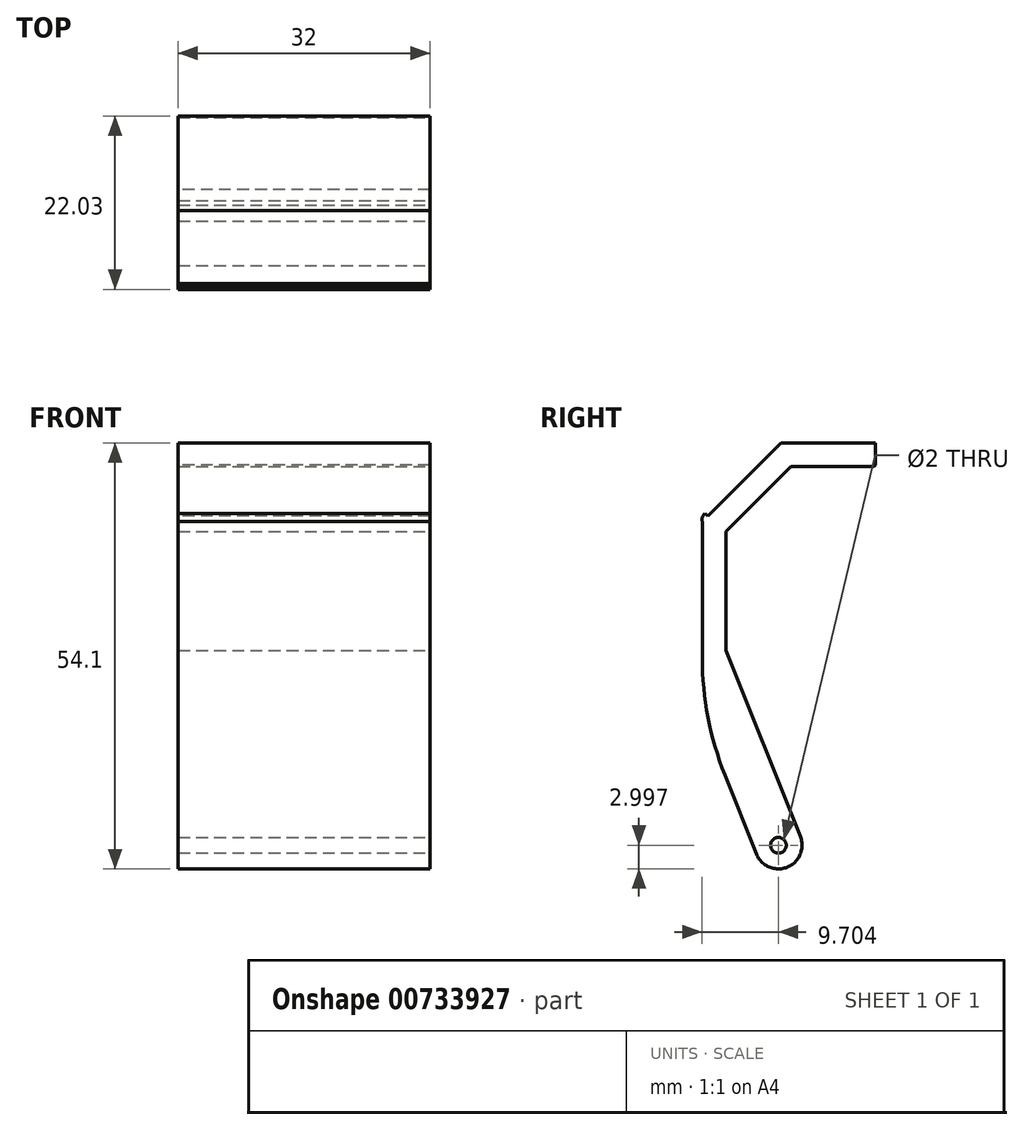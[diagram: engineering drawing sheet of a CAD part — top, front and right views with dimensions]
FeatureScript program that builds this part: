
annotation { "Feature Type Name" : "Feature", "Feature Type Description" : "" }
export const myFeature = defineFeature(function(context is Context, id is Id, definition is map)
    precondition{}
    {
        {
            var Q0;
            Q0=qCreatedBy(makeId("Right.planeOp"),FACE);
            var sketch = newSketch(context, id + "F0", { "sketchPlane" : qUnion([Q0])});
            skLineSegment(sketch, "E0.bottom", {"start": v(43.74, 41.65) * mm, "end": v(40.74, 41.65) * mm});
            skLineSegment(sketch, "E0.top", {"start": v(43.74, 21.65) * mm, "end": v(40.74, 21.65) * mm});
            skLineSegment(sketch, "E0.left", {"start": v(43.74, 41.65) * mm, "end": v(43.74, 21.65) * mm});
            skLineSegment(sketch, "E0.right", {"start": v(40.74, 41.65) * mm, "end": v(40.74, 21.65) * mm});
            skSolve(sketch);
        }
        {
            var Q0;
            Q0=makeQuery(id+"F0.imprint","IMPRINT",FACE,{"disambiguationData":[TD([[makeQuery(id+"F0.imprint","IMPRINT",EDGE,{"derivedFrom":sQuery(id+"F0.wireOp",EDGE,"E0.bottom")}),1.0]])]});
            extrude(context, id + "F1", {"entities" : qUnion([Q0]), "depth" : 10 * mm, "offsetDistance" : 25 * mm});
        }
        {
            var Q0;
            Q0=makeQuery(id+"F1.opExtrude","CAP_FACE",FACE,{"disambiguationData":[OSD([sQuery(id+"F0.wireOp",EDGE,"E0.bottom"),sQuery(id+"F0.wireOp",EDGE,"E0.top"),sQuery(id+"F0.wireOp",EDGE,"E0.left"),sQuery(id+"F0.wireOp",EDGE,"E0.right")])],"isStart":true});
            var sketch = newSketch(context, id + "F2", { "sketchPlane" : qUnion([Q0])});
            skLineSegment(sketch, "E1.bottom", {"start": v(-43.74, 41.65) * mm, "end": v(-18.74, 41.65) * mm});
            skLineSegment(sketch, "E1.top", {"start": v(-43.74, -18.35) * mm, "end": v(-18.74, -18.35) * mm});
            skLineSegment(sketch, "E1.left", {"start": v(-43.74, 41.65) * mm, "end": v(-43.74, -18.35) * mm});
            skLineSegment(sketch, "E1.right", {"start": v(-18.74, 41.65) * mm, "end": v(-18.74, -18.35) * mm});
            skLineSegment(sketch, "E2", {"start": v(-28.74, -18.35) * mm, "end": v(-18.74, 6.65) * mm});
            skLineSegment(sketch, "E3", {"start": v(-28.74, 41.65) * mm, "end": v(-18.74, 31.65) * mm});
            skSolve(sketch);
        }
        {
            var Q0;
            {var subQ4=makeQuery(id+"F1.opExtrude","CAP_EDGE",EDGE,{"disambiguationData":[OSD([sQuery(id+"F0.wireOp",EDGE,"E0.top")])],"isStart":true});Q0=makeQuery(id+"F2.imprint","IMPRINT",FACE,{"disambiguationData":[TD([[makeQuery(id+"F2.imprint","IMPRINT",EDGE,{"derivedFrom":subQ4}),1.0]])]});}
            var Q1;
            {var subQ3=sQuery(id+"F2.wireOp",EDGE,"E2");Q1=makeQuery(id+"F2.imprint","IMPRINT",FACE,{"disambiguationData":[TD([[makeQuery(id+"F2.imprint","IMPRINT",EDGE,{"derivedFrom":subQ3}),1.0]])]});}
            extrude(context, id + "F3", {"entities" : qUnion([Q0, Q1]), "operationType" : NewBodyOperationType.ADD, "depth" : 3 * mm, "offsetDistance" : 25 * mm});
        }
        {
            var Q0;
            Q0=makeQuery(id+"F1.opExtrude","CAP_FACE",FACE,{"disambiguationData":[OSD([sQuery(id+"F0.wireOp",EDGE,"E0.bottom"),sQuery(id+"F0.wireOp",EDGE,"E0.top"),sQuery(id+"F0.wireOp",EDGE,"E0.left"),sQuery(id+"F0.wireOp",EDGE,"E0.right")])],"isStart":false});
            extrude(context, id + "F4", {"entities" : qUnion([Q0]), "operationType" : NewBodyOperationType.REMOVE, "oppositeDirection" : true, "depth" : 10 * mm, "offsetDistance" : 25 * mm});
        }
        {
            var Q0;
            Q0=makeQuery(id+"F4.boolean.opBoolean","MERGE",FACE,{"derivedFrom":[makeQuery(id+"F3.opExtrude","CAP_FACE",FACE,{"disambiguationData":[OSD([sQuery(id+"F2.wireOp",EDGE,"E1.bottom"),sQuery(id+"F2.wireOp",EDGE,"E1.top"),sQuery(id+"F2.wireOp",EDGE,"E1.left"),sQuery(id+"F2.wireOp",EDGE,"E1.right"),sQuery(id+"F2.wireOp",EDGE,"E2"),sQuery(id+"F2.wireOp",EDGE,"E3")])],"isStart":true}),makeQuery(id+"F4.opExtrude","CAP_FACE",FACE,{"disambiguationData":[OSD([sQuery(id+"F0.wireOp",EDGE,"E0.bottom"),sQuery(id+"F0.wireOp",EDGE,"E0.top"),sQuery(id+"F0.wireOp",EDGE,"E0.left"),sQuery(id+"F0.wireOp",EDGE,"E0.right")])],"isStart":false})]});
            var sketch = newSketch(context, id + "F5", { "sketchPlane" : qUnion([Q0])});
            skLineSegment(sketch, "E4", {"start": v(26.74, -13.35) * mm, "end": v(43.74, -13.35) * mm});
            skLineSegment(sketch, "E5.bottom", {"start": v(43.74, 41.65) * mm, "end": v(40.74, 41.65) * mm});
            skLineSegment(sketch, "E5.top", {"start": v(43.74, 21.65) * mm, "end": v(40.74, 21.65) * mm});
            skLineSegment(sketch, "E5.left", {"start": v(43.74, 41.65) * mm, "end": v(43.74, 21.65) * mm});
            skLineSegment(sketch, "E5.right", {"start": v(40.74, 41.65) * mm, "end": v(40.74, 21.65) * mm});
            skLineSegment(sketch, "E6", {"start": v(25.74, 38.65) * mm, "end": v(40.74, 38.65) * mm});
            skLineSegment(sketch, "E7", {"start": v(21.74, 34.65) * mm, "end": v(21.74, -0.85) * mm});
            skLineSegment(sketch, "E8", {"start": v(28.74, 41.65) * mm, "end": v(18.74, 31.65) * mm});
            skLineSegment(sketch, "E9", {"start": v(28.74, 41.65) * mm, "end": v(34.27, 36.12) * mm});
            skLineSegment(sketch, "E10", {"start": v(18.74, 31.65) * mm, "end": v(24.45, 25.94) * mm});
            skLineSegment(sketch, "E11", {"start": v(30.86, 39.53) * mm, "end": v(20.86, 29.53) * mm});
            skLineSegment(sketch, "E12", {"start": v(18.74, 6.65) * mm, "end": v(27.56, 10.17) * mm});
            skLineSegment(sketch, "E13", {"start": v(28.74, -18.35) * mm, "end": v(44.97, -11.86) * mm});
            skLineSegment(sketch, "E14", {"start": v(24.31, 8.88) * mm, "end": v(34.31, -16.12) * mm});
            skLineSegment(sketch, "E15", {"start": v(26.74, -13.35) * mm, "end": v(32.31, -11.12) * mm});
            skLineSegment(sketch, "E16", {"start": v(24.31, 8.88) * mm, "end": v(21.74, 15.3) * mm});
            skSolve(sketch);
        }
        {
            var Q0;
            {var subQ0=sQuery(id+"F5.wireOp",EDGE,"E4");Q0=makeQuery(id+"F5.imprint","IMPRINT",FACE,{"disambiguationData":[TD([[makeQuery(id+"F5.imprint","IMPRINT",EDGE,{"derivedFrom":subQ0}),-1.0]])]});}
            var Q1;
            Q1=makeQuery(id+"F5.imprint","IMPRINT",FACE,{"disambiguationData":[TD([[makeQuery(id+"F5.imprint","IMPRINT",EDGE,{"derivedFrom":sQuery(id+"F5.wireOp",EDGE,"E5.bottom")}),1.0]])]});
            var Q2;
            {var subQ0=makeQuery(id+"F3.opExtrude","CAP_EDGE",EDGE,{"disambiguationData":[OSD([sQuery(id+"F2.wireOp",EDGE,"E1.top")])],"isStart":true});Q2=makeQuery(id+"F5.imprint","IMPRINT",FACE,{"disambiguationData":[TD([[makeQuery(id+"F5.imprint","IMPRINT",EDGE,{"derivedFrom":subQ0}),-1.0]])]});}
            var Q3;
            {var subQ0=sQuery(id+"F5.wireOp",EDGE,"E4");var subQ1=makeQuery(id+"F3.opExtrude","CAP_EDGE",EDGE,{"disambiguationData":[OSD([sQuery(id+"F2.wireOp",EDGE,"E2")])],"isStart":true});var subQ2=makeQuery(id+"F5.imprint","INTERSECT",VERTEX,{"derivedFrom":[subQ1,subQ0]});Q3=makeQuery(id+"F5.imprint","IMPRINT",FACE,{"disambiguationData":[TD([[makeQuery(id+"F5.imprint","IMPRINT",EDGE,{"disambiguationData":[TD([[subQ2,-1.0]])],"derivedFrom":subQ0}),-1.0]])]});}
            var Q4;
            {var subQ6=sQuery(id+"F5.wireOp",EDGE,"E5.top");Q4=makeQuery(id+"F5.imprint","IMPRINT",FACE,{"disambiguationData":[TD([[makeQuery(id+"F5.imprint","IMPRINT",EDGE,{"derivedFrom":subQ6}),1.0]])]});}
            var Q5;
            {var subQ0=sQuery(id+"F5.wireOp",EDGE,"E4");var subQ3=sQuery(id+"F5.wireOp",EDGE,"E13");var subQ4=makeQuery(id+"F5.imprint","INTERSECT",VERTEX,{"derivedFrom":[subQ0,subQ3]});Q5=makeQuery(id+"F5.imprint","IMPRINT",FACE,{"disambiguationData":[TD([[makeQuery(id+"F5.imprint","IMPRINT",EDGE,{"disambiguationData":[TD([[subQ4,-1.0]])],"derivedFrom":subQ0}),1.0]])]});}
            var Q6;
            {var subQ0=sQuery(id+"F5.wireOp",EDGE,"E15");Q6=makeQuery(id+"F5.imprint","IMPRINT",FACE,{"disambiguationData":[TD([[makeQuery(id+"F5.imprint","IMPRINT",EDGE,{"derivedFrom":subQ0}),-1.0]])]});}
            extrude(context, id + "F6", {"entities" : qUnion([Q0, Q1, Q2, Q3, Q4, Q5, Q6]), "operationType" : NewBodyOperationType.REMOVE, "oppositeDirection" : true, "depth" : 25 * mm, "offsetDistance" : 25 * mm});
        }
        {
            var Q0;
            Q0=makeQuery(id+"F4.boolean.opBoolean","MERGE",FACE,{"derivedFrom":[makeQuery(id+"F3.opExtrude","CAP_FACE",FACE,{"disambiguationData":[OSD([sQuery(id+"F2.wireOp",EDGE,"E1.bottom"),sQuery(id+"F2.wireOp",EDGE,"E1.top"),sQuery(id+"F2.wireOp",EDGE,"E1.left"),sQuery(id+"F2.wireOp",EDGE,"E1.right"),sQuery(id+"F2.wireOp",EDGE,"E2"),sQuery(id+"F2.wireOp",EDGE,"E3")])],"isStart":true}),makeQuery(id+"F4.opExtrude","CAP_FACE",FACE,{"disambiguationData":[OSD([sQuery(id+"F0.wireOp",EDGE,"E0.bottom"),sQuery(id+"F0.wireOp",EDGE,"E0.top"),sQuery(id+"F0.wireOp",EDGE,"E0.left"),sQuery(id+"F0.wireOp",EDGE,"E0.right")])],"isStart":false})]});
            extrude(context, id + "F7", {"entities" : qUnion([Q0]), "operationType" : NewBodyOperationType.ADD, "depth" : 29 * mm, "offsetDistance" : 25 * mm});
        }
        {
            var Q0;
            {var subQ0=sQuery(id+"F5.wireOp",EDGE,"E15");var subQ1=sQuery(id+"F5.wireOp",EDGE,"E4");var subQ2=sQuery(id+"F2.wireOp",EDGE,"E2");Q0=makeQuery(id+"F7.boolean.opBoolean","MERGE",EDGE,{"derivedFrom":[makeQuery(id+"F6.boolean.opBoolean","COPY",EDGE,{"derivedFrom":makeQuery(id+"F6.opExtrude","SWEPT_EDGE",EDGE,{"disambiguationData":[OSD([subQ2,subQ1,subQ0])]})}),makeQuery(id+"F7.opExtrude","SWEPT_EDGE",EDGE,{"disambiguationData":[OSD([subQ2,subQ1,subQ0])]})]});}
            var Q1;
            {var subQ0=sQuery(id+"F5.wireOp",EDGE,"E15");var subQ1=sQuery(id+"F5.wireOp",EDGE,"E14");Q1=makeQuery(id+"F7.boolean.opBoolean","MERGE",EDGE,{"derivedFrom":[makeQuery(id+"F6.boolean.opBoolean","COPY",EDGE,{"derivedFrom":makeQuery(id+"F6.opExtrude","SWEPT_EDGE",EDGE,{"disambiguationData":[OSD([subQ1,subQ0])]})}),makeQuery(id+"F7.opExtrude","SWEPT_EDGE",EDGE,{"disambiguationData":[OSD([subQ1,subQ0])]})]});}
            fillet(context, id + "F8", {"entities" : qUnion([Q0, Q1]), "radius" : 3 * mm, "tangentPropagation" : true, "allowEdgeOverflow" : false});
        }
        {
            var Q0;
            Q0=makeQuery(id+"F7.opExtrude","CAP_FACE",FACE,{"disambiguationData":[OSD([sQuery(id+"F0.wireOp",EDGE,"E0.bottom"),sQuery(id+"F0.wireOp",EDGE,"E0.top"),sQuery(id+"F0.wireOp",EDGE,"E0.left"),sQuery(id+"F0.wireOp",EDGE,"E0.right"),sQuery(id+"F2.wireOp",EDGE,"E1.bottom"),sQuery(id+"F2.wireOp",EDGE,"E1.top"),sQuery(id+"F2.wireOp",EDGE,"E1.left"),sQuery(id+"F2.wireOp",EDGE,"E1.right"),sQuery(id+"F2.wireOp",EDGE,"E2"),sQuery(id+"F2.wireOp",EDGE,"E3")])],"isStart":false});
            var sketch = newSketch(context, id + "F9", { "sketchPlane" : qUnion([Q0])});
            skCircle(sketch, "E17", {"center": v(28.41, -9.45) * mm, "radius": 1 * mm});
            skSolve(sketch);
        }
        {
            var Q0;
            Q0=makeQuery(id+"F9.imprint","IMPRINT",FACE,{"disambiguationData":[TD([[makeQuery(id+"F9.imprint","IMPRINT",EDGE,{"derivedFrom":sQuery(id+"F9.wireOp",EDGE,"E17")}),1.0]])]});
            extrude(context, id + "F10", {"entities" : qUnion([Q0]), "operationType" : NewBodyOperationType.REMOVE, "oppositeDirection" : true, "depth" : 100 * mm, "offsetDistance" : 25 * mm});
        }
        {
            var Q0;
            {var subQ0=sQuery(id+"F2.wireOp",EDGE,"E2");var subQ1=sQuery(id+"F2.wireOp",EDGE,"E1.right");Q0=makeQuery(id+"F7.boolean.opBoolean","MERGE",EDGE,{"derivedFrom":[makeQuery(id+"F3.opExtrude","SWEPT_EDGE",EDGE,{"disambiguationData":[OSD([subQ1,subQ0])]}),makeQuery(id+"F7.opExtrude","SWEPT_EDGE",EDGE,{"disambiguationData":[OSD([subQ1,subQ0])]})]});}
            fillet(context, id + "F11", {"entities" : qUnion([Q0]), "radius" : 40 * mm, "tangentPropagation" : true, "allowEdgeOverflow" : false});
        }
        {
            var Q0;
            {var subQ0=sQuery(id+"F2.wireOp",EDGE,"E3");Q0=makeQuery(id+"F7.boolean.opBoolean","MERGE",FACE,{"derivedFrom":[makeQuery(id+"F3.opExtrude","SWEPT_FACE",FACE,{"disambiguationData":[OSD([subQ0])]}),makeQuery(id+"F7.opExtrude","SWEPT_FACE",FACE,{"disambiguationData":[OSD([subQ0])]})]});}
            var sketch = newSketch(context, id + "F12", { "sketchPlane" : qUnion([Q0])});
            skLineSegment(sketch, "E18.bottom", {"start": v(29, 35.63) * mm, "end": v(-3, 35.63) * mm});
            skLineSegment(sketch, "E18.top", {"start": v(29, 36.63) * mm, "end": v(-3, 36.63) * mm});
            skLineSegment(sketch, "E18.left", {"start": v(29, 35.63) * mm, "end": v(29, 36.63) * mm});
            skLineSegment(sketch, "E18.right", {"start": v(-3, 35.63) * mm, "end": v(-3, 36.63) * mm});
            skSolve(sketch);
        }
        {
            var Q0;
            Q0=makeQuery(id+"F12.imprint","IMPRINT",FACE,{"disambiguationData":[TD([[makeQuery(id+"F12.imprint","IMPRINT",EDGE,{"derivedFrom":sQuery(id+"F12.wireOp",EDGE,"E18.bottom")}),1.0]])]});
            extrude(context, id + "F13", {"entities" : qUnion([Q0]), "operationType" : NewBodyOperationType.ADD, "depth" : .5 * mm, "offsetDistance" : 25 * mm});
        }
        {
            var Q0;
            Q0=makeQuery(id+"F13.opExtrude","CAP_EDGE",EDGE,{"disambiguationData":[OSD([sQuery(id+"F12.wireOp",EDGE,"E18.bottom")])],"isStart":false});
            fillet(context, id + "F14", {"entities" : qUnion([Q0]), "radius" : 1 * mm, "tangentPropagation" : true, "allowEdgeOverflow" : false});
        }
        {
            var Q0;
            {var subQ0=sQuery(id+"F5.wireOp",EDGE,"E6");var subQ1=sQuery(id+"F5.wireOp",EDGE,"E5.right");Q0=makeQuery(id+"F7.boolean.opBoolean","MERGE",EDGE,{"derivedFrom":[makeQuery(id+"F6.boolean.opBoolean","COPY",EDGE,{"derivedFrom":makeQuery(id+"F6.opExtrude","SWEPT_EDGE",EDGE,{"disambiguationData":[OSD([subQ1,subQ0])]})}),makeQuery(id+"F7.opExtrude","SWEPT_EDGE",EDGE,{"disambiguationData":[OSD([subQ1,subQ0])]})]});}
            chamfer(context, id + "F15", {"entities" : qUnion([Q0]), "width" : .2 * mm, "tangentPropagation" : true});
        }
    });
